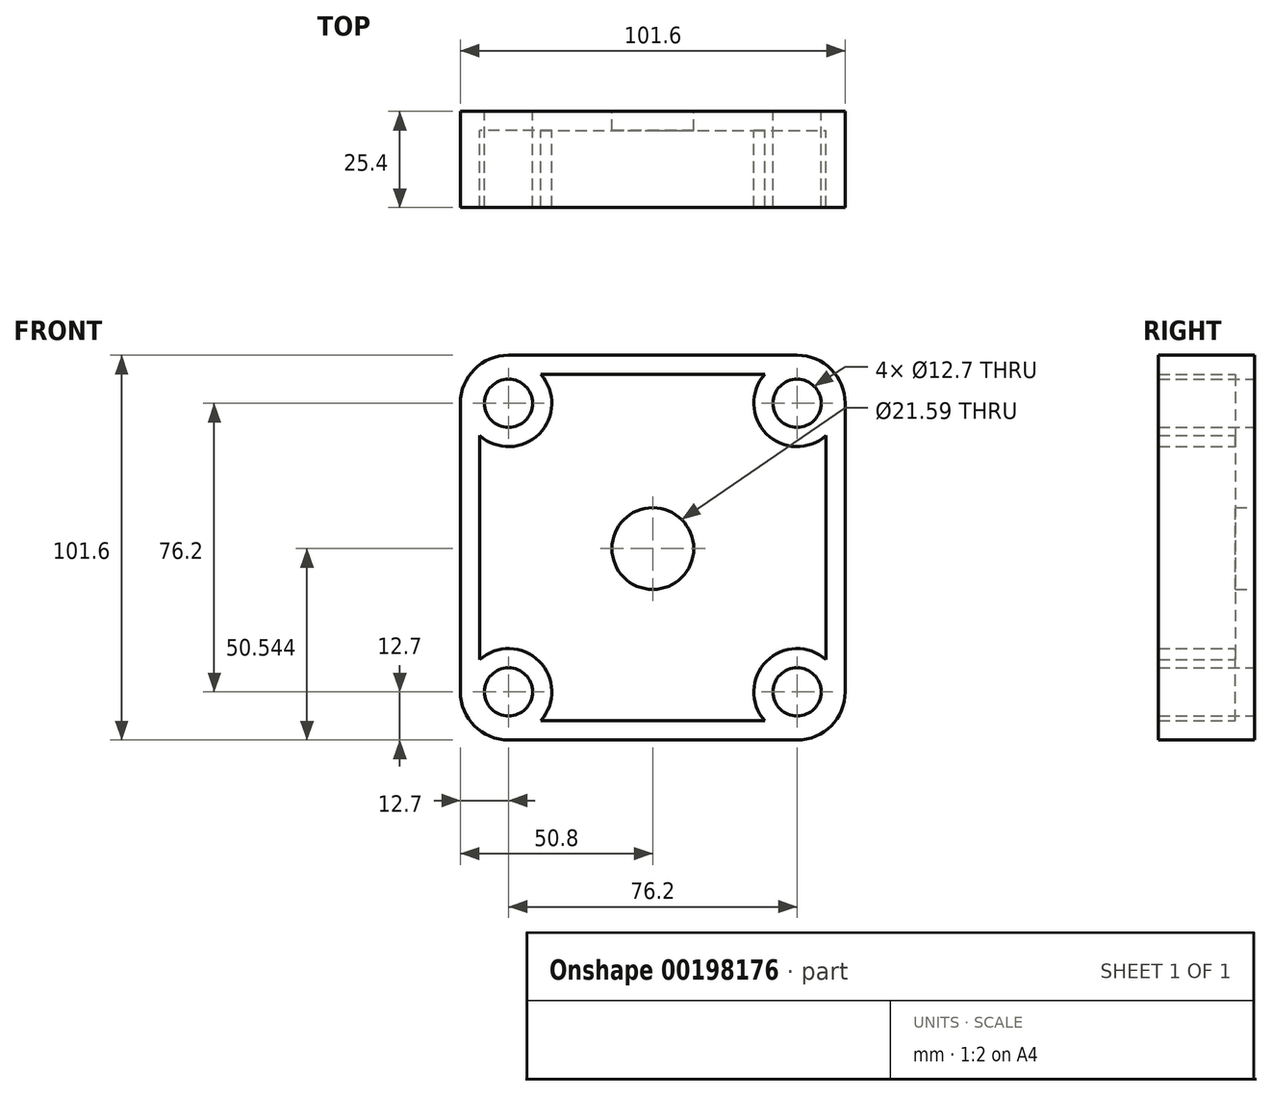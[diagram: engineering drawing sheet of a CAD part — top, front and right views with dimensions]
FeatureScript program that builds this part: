
annotation { "Feature Type Name" : "Feature", "Feature Type Description" : "" }
export const myFeature = defineFeature(function(context is Context, id is Id, definition is map)
    precondition{}
    {
        {
            var Q0;
            Q0=qCreatedBy(makeId("Front.planeOp"),FACE);
            var sketch = newSketch(context, id + "F0", { "sketchPlane" : qUnion([Q0])});
            skLineSegment(sketch, "E0.bottom", {"start": v(-50.8, 63.5) * mm, "end": v(50.8, 63.5) * mm});
            skLineSegment(sketch, "E0.top", {"start": v(-50.8, -38.1) * mm, "end": v(50.8, -38.1) * mm});
            skLineSegment(sketch, "E0.left", {"start": v(-50.8, 63.5) * mm, "end": v(-50.8, -38.1) * mm});
            skLineSegment(sketch, "E0.right", {"start": v(50.8, 63.5) * mm, "end": v(50.8, -38.1) * mm});
            skCircle(sketch, "E1", {"center": v(-38.1, 50.8) * mm, "radius": 6.35 * mm});
            skCircle(sketch, "E2", {"center": v(38.1, 50.8) * mm, "radius": 6.35 * mm});
            skLineSegment(sketch, "E3", {"start": v(50.8, 12.7) * mm, "end": v(-50.8, 12.7) * mm, "construction": true});
            skCircle(sketch, "E4.MirrorC", {"center": v(-38.1, -25.4) * mm, "radius": 6.35 * mm});
            skCircle(sketch, "E5.MirrorC", {"center": v(38.1, -25.4) * mm, "radius": 6.35 * mm});
            skCircle(sketch, "E6", {"center": v(0, 71.44) * mm, "radius": 36.98 * mm});
            skPoint(sketch, "E7", {"position": v(0, 63.5) * mm});
            skLineSegment(sketch, "E8", {"start": v(0, 63.5) * mm, "end": v(0, 108.42) * mm});
            skLineSegment(sketch, "E9", {"start": v(0, 63.5) * mm, "end": v(-36.12, 63.5) * mm});
            skSolve(sketch);
        }
        {
            var Q0;
            {var subQ0=sQuery(id+"F0.wireOp",EDGE,"E6");var subQ1=sQuery(id+"F0.wireOp",EDGE,"E0.bottom");var subQ2=makeQuery(id+"F0.imprint","INTERSECT",VERTEX,{"disambiguationData":[OD(0.0)],"derivedFrom":[subQ1,subQ0]});Q0=makeQuery(id+"F0.imprint","IMPRINT",FACE,{"disambiguationData":[TD([[makeQuery(id+"F0.imprint","IMPRINT",EDGE,{"disambiguationData":[TD([[subQ2,-1.0]])],"derivedFrom":subQ1}),-1.0]])]});}
            var Q1;
            Q1=makeQuery(id+"F0.imprint","IMPRINT",FACE,{"disambiguationData":[TD([[makeQuery(id+"F0.imprint","IMPRINT",EDGE,{"derivedFrom":sQuery(id+"F0.wireOp",EDGE,"E0.top")}),1.0]])]});
            var Q2;
            {var subQ5=sQuery(id+"F0.wireOp",EDGE,"E9");Q2=makeQuery(id+"F0.imprint","IMPRINT",FACE,{"disambiguationData":[TD([[makeQuery(id+"F0.imprint","IMPRINT",EDGE,{"derivedFrom":subQ5}),1.0]])]});}
            extrude(context, id + "F1", {"entities" : qUnion([Q0, Q1, Q2]), "depth" : 25.4 * mm});
        }
        {
            var Q0;
            Q0=makeQuery(id+"F1.opExtrude","SWEPT_EDGE",EDGE,{"disambiguationData":[OSD([sQuery(id+"F0.wireOp",EDGE,"E0.top"),sQuery(id+"F0.wireOp",EDGE,"E0.left")])]});
            var Q1;
            Q1=makeQuery(id+"F1.opExtrude","SWEPT_EDGE",EDGE,{"disambiguationData":[OSD([sQuery(id+"F0.wireOp",EDGE,"E0.top"),sQuery(id+"F0.wireOp",EDGE,"E0.right")])]});
            fillet(context, id + "F2", {"entities" : qUnion([Q0, Q1]), "radius" : 12.7 * mm, "tangentPropagation" : true, "allowEdgeOverflow" : false});
        }
        {
            var Q0;
            Q0=makeQuery(id+"F1.opExtrude","SWEPT_EDGE",EDGE,{"disambiguationData":[OSD([sQuery(id+"F0.wireOp",EDGE,"E0.bottom"),sQuery(id+"F0.wireOp",EDGE,"E0.left")])]});
            var Q1;
            Q1=makeQuery(id+"F1.opExtrude","SWEPT_EDGE",EDGE,{"disambiguationData":[OSD([sQuery(id+"F0.wireOp",EDGE,"E0.bottom"),sQuery(id+"F0.wireOp",EDGE,"E0.right")])]});
            fillet(context, id + "F3", {"entities" : qUnion([Q0, Q1]), "radius" : 12.7 * mm, "tangentPropagation" : true, "allowEdgeOverflow" : false});
        }
        {
            var Q0;
            Q0=makeQuery(id+"F1.opExtrude","CAP_FACE",FACE,{"disambiguationData":[OSD([sQuery(id+"F0.wireOp",EDGE,"E0.bottom"),sQuery(id+"F0.wireOp",EDGE,"E0.top"),sQuery(id+"F0.wireOp",EDGE,"E0.left"),sQuery(id+"F0.wireOp",EDGE,"E0.right"),sQuery(id+"F0.wireOp",EDGE,"E1"),sQuery(id+"F0.wireOp",EDGE,"E2"),sQuery(id+"F0.wireOp",EDGE,"E4.MirrorC"),sQuery(id+"F0.wireOp",EDGE,"E5.MirrorC"),sQuery(id+"F0.wireOp",EDGE,"E9")])],"isStart":false});
            shell(context, id + "F4", {"entities" : qUnion([Q0]), "thickness" : 5.08 * mm});
        }
        {
            var Q0;
            Q0=makeQuery(id+"F0.imprint","IMPRINT",FACE,{"disambiguationData":[TD([[makeQuery(id+"F0.imprint","IMPRINT",EDGE,{"derivedFrom":sQuery(id+"F0.wireOp",EDGE,"E0.bottom")}),-1.0]])]});
            var sketch = newSketch(context, id + "F6", { "sketchPlane" : qUnion([Q0])});
            skCircle(sketch, "E10", {"center": v(0, 12.44) * mm, "radius": 10.8 * mm});
            skLineSegment(sketch, "E11", {"start": v(0, 63.22) * mm, "end": v(0, -38.33) * mm, "construction": true});
            skLineSegment(sketch, "E12", {"start": v(0, -38.33) * mm, "end": v(20.64, -13.94) * mm, "construction": true});
            skSolve(sketch);
        }
        {
            var Q0;
            Q0=makeQuery(id+"F6.imprint","IMPRINT",FACE,{"disambiguationData":[TD([[makeQuery(id+"F6.imprint","IMPRINT",EDGE,{"derivedFrom":sQuery(id+"F6.wireOp",EDGE,"E10")}),1.0]])]});
            var Q1;
            Q1=makeQuery(id+"F4.opShell","OFFSET_FACE",FACE,{"disambiguationData":[OSD([sQuery(id+"F0.wireOp",EDGE,"E0.bottom"),sQuery(id+"F0.wireOp",EDGE,"E0.top"),sQuery(id+"F0.wireOp",EDGE,"E0.left"),sQuery(id+"F0.wireOp",EDGE,"E0.right"),sQuery(id+"F0.wireOp",EDGE,"E1"),sQuery(id+"F0.wireOp",EDGE,"E2"),sQuery(id+"F0.wireOp",EDGE,"E4.MirrorC"),sQuery(id+"F0.wireOp",EDGE,"E5.MirrorC")])]});
            extrude(context, id + "F5", {"entities" : qUnion([Q0]), "operationType" : NewBodyOperationType.REMOVE, "endBound" : BoundingType.UP_TO_SURFACE, "endBoundEntityFace" : qUnion([Q1]), "depth" : 25.4 * mm});
        }
    });
